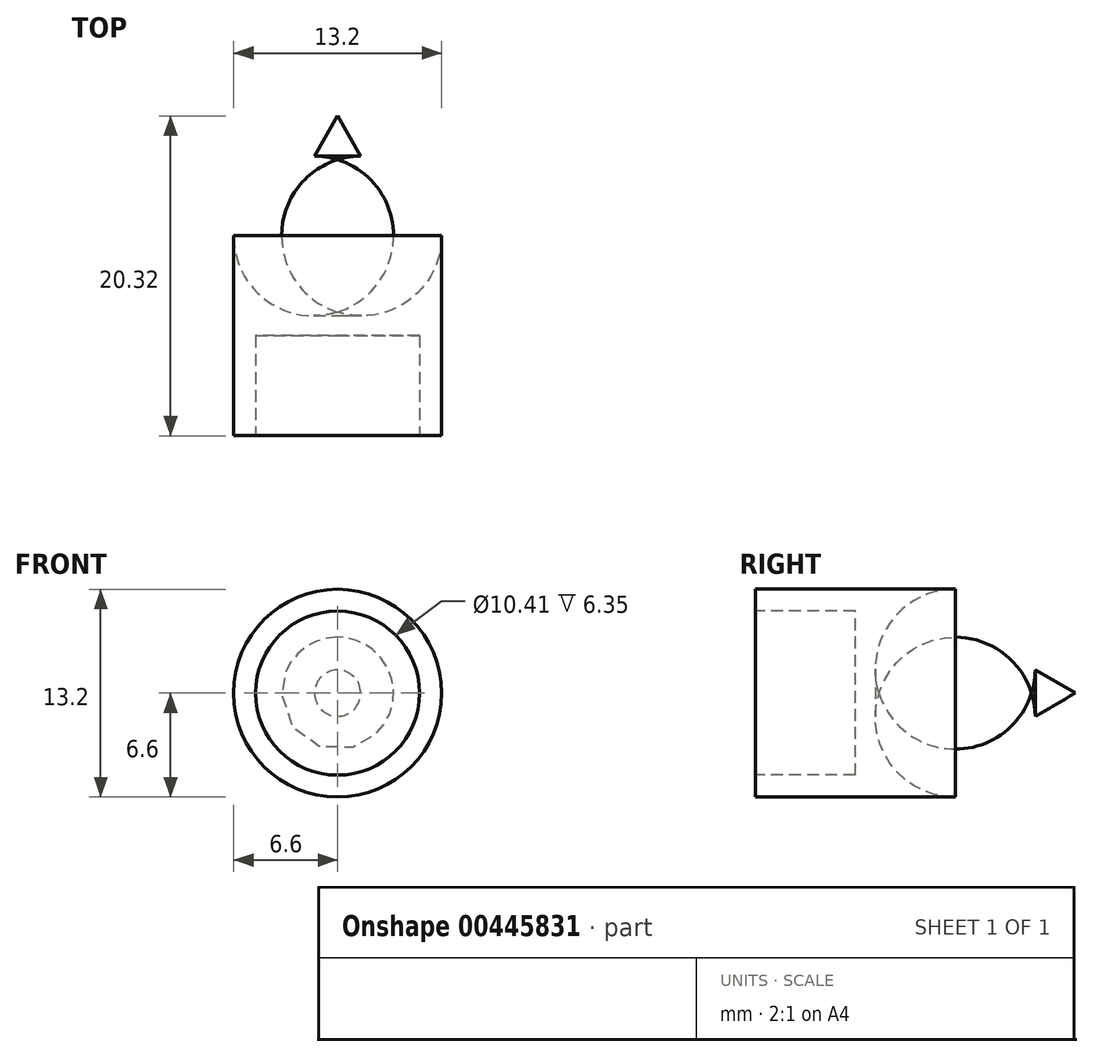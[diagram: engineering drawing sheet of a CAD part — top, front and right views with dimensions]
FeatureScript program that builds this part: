
annotation { "Feature Type Name" : "Feature", "Feature Type Description" : "" }
export const myFeature = defineFeature(function(context is Context, id is Id, definition is map)
    precondition{}
    {
        {
            var Q0;
            Q0=qCreatedBy(makeId("Top.planeOp"),FACE);
            var sketch = newSketch(context, id + "F0", { "sketchPlane" : qUnion([Q0])});
            skLineSegment(sketch, "E0", {"start": v(0, 0) * mm, "end": v(0, 25.4) * mm});
            skLineSegment(sketch, "E1.bottom", {"start": v(0, 21.7) * mm, "end": v(6.6, 21.7) * mm});
            skLineSegment(sketch, "E1.top", {"start": v(0, 3.91) * mm, "end": v(6.6, 3.91) * mm});
            skLineSegment(sketch, "E1.left", {"start": v(0, 21.7) * mm, "end": v(0, 3.91) * mm});
            skLineSegment(sketch, "E1.right", {"start": v(6.6, 21.7) * mm, "end": v(6.6, 3.91) * mm});
            skSolve(sketch);
        }
        {
            var Q0;
            Q0=makeQuery(id+"F0.imprint","IMPRINT",FACE,{"disambiguationData":[TD([[makeQuery(id+"F0.imprint","IMPRINT",EDGE,{"derivedFrom":sQuery(id+"F0.wireOp",EDGE,"E1.bottom")}),-1.0]])]});
            var Q1;
            Q1=sQuery(id+"F0.wireOp",EDGE,"E0");
            revolve(context, id + "F1", {"entities" : qUnion([Q0]), "axis" : qUnion([Q1]), "revolveType" : RevolveType.FULL});
        }
        {
            var Q0;
            Q0=makeQuery(id+"F1.opRevolve","SWEPT_EDGE",EDGE,{"disambiguationData":[OSD([sQuery(id+"F0.wireOp",EDGE,"E1.bottom"),sQuery(id+"F0.wireOp",EDGE,"E1.right")])]});
            fillet(context, id + "F2", {"entities" : qUnion([Q0]), "radius" : 5.08 * mm, "tangentPropagation" : true, "allowEdgeOverflow" : false});
        }
        {
            var Q0;
            Q0=makeQuery(id+"F1.opRevolve","SWEPT_FACE",FACE,{"disambiguationData":[OSD([sQuery(id+"F0.wireOp",EDGE,"E1.bottom")])]});
            extrude(context, id + "F3", {"entities" : qUnion([Q0]), "operationType" : NewBodyOperationType.ADD, "depth" : 2.54 * mm});
        }
        {
            var Q0;
            Q0=makeQuery(id+"F3.opExtrude","CAP_EDGE",EDGE,{"disambiguationData":[OSD([sQuery(id+"F0.wireOp",EDGE,"E1.bottom"),sQuery(id+"F0.wireOp",EDGE,"E1.right")])],"isStart":false});
            chamfer(context, id + "F4", {"entities" : qUnion([Q0]), "chamferType" : ChamferType.OFFSET_ANGLE, "width" : 1.52 * mm, "oppositeDirection" : false, "angle" : 60 * degree, "tangentPropagation" : true});
        }
        {
            var Q0;
            Q0=makeQuery(id+"F1.opRevolve","SWEPT_FACE",FACE,{"disambiguationData":[OSD([sQuery(id+"F0.wireOp",EDGE,"E1.top")])]});
            var sketch = newSketch(context, id + "F5", { "sketchPlane" : qUnion([Q0])});
            skCircle(sketch, "E2", {"center": v(0, 0) * mm, "radius": 5.2 * mm});
            skSolve(sketch);
        }
        {
            var Q0;
            Q0=makeQuery(id+"F5.imprint","IMPRINT",FACE,{"disambiguationData":[TD([[makeQuery(id+"F5.imprint","IMPRINT",EDGE,{"derivedFrom":sQuery(id+"F5.wireOp",EDGE,"E2")}),1.0]])]});
            extrude(context, id + "F6", {"entities" : qUnion([Q0]), "operationType" : NewBodyOperationType.REMOVE, "oppositeDirection" : true, "depth" : 6.35 * mm});
        }
    });
